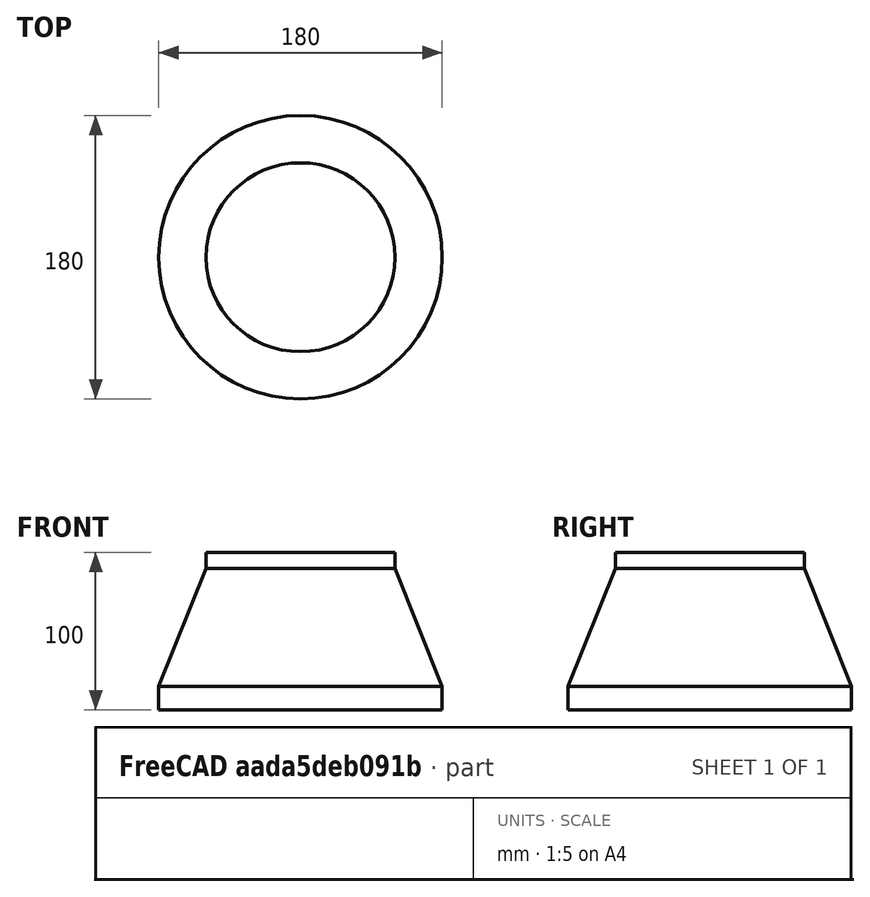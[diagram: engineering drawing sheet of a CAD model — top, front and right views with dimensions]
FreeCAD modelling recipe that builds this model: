
FCSTD DOCUMENT  (FreeCAD 0.19R24366 (Git))
Label: link_0
License: All rights reserved
LicenseURL: http://en.wikipedia.org/wiki/All_rights_reserved
objects: Sketcher::SketchObject×1, PartDesign::Revolution×1, PartDesign::Body×1, Mesh::Feature×1
note: 4 computed .brp shape members not serialized (recipe doc carries the construction recipe); baked Part::Feature solids carry a one-line shape summary decoded from their .brp

FEATURE [Sketcher::SketchObject] Sketch
  FullyConstrained = true
  MapMode = 5
  Placement = pos=(0,0,0) rot=(1,0,0;1.5708rad)
  Support = -> [XZ_Plane]
  sketch-geometry (6):
    g0: LineSegment StartX=1e-16 StartY=50 StartZ=0 EndX=0 EndY=-50 EndZ=0
    g1: LineSegment StartX=1e-16 StartY=50 StartZ=0 EndX=60 EndY=50 EndZ=0
    g2: LineSegment StartX=60 StartY=50 StartZ=0 EndX=60 EndY=40 EndZ=0
    g3: LineSegment StartX=0 StartY=-50 StartZ=0 EndX=90 EndY=-50 EndZ=0
    g4: LineSegment StartX=90 StartY=-50 StartZ=0 EndX=90 EndY=-35 EndZ=0
    g5: LineSegment StartX=90 StartY=-35 StartZ=0 EndX=60 EndY=40 EndZ=0
  constraints (17):
    c: Symmetric(g0,g0,g-1)
    c: PointOnObject(g0,g-2)
    c: DistanceY(g0,g0) = 100
    c: Coincident(g1,g0)
    c: Horizontal(g1)
    c: DistanceX(g1,g1) = 60
    c: Coincident(g2,g1)
    c: Vertical(g2)
    c: Horizontal(g3)
    c: Vertical(g4)
    c: Coincident(g5,g2)
    c: DistanceX(g3,g3) = 90
    c: Coincident(g3,g0)
    c: Coincident(g4,g3)
    c: Coincident(g5,g4)
    c: DistanceY(g2,g2) = 10
    c: DistanceY(g4,g4) = 15
FEATURE [PartDesign::Revolution] Revolution
  AllowMultiFace = false
  Angle = 360
  Axis = (0,-2e-16,1)
  Base = (0,0,0)
  Placement = pos=(0,0,0) rot=(1,0,0;1.5708rad)
  Profile = -> Sketch
  ReferenceAxis = -> Sketch [V_Axis]
  Reversed = true
FEATURE [PartDesign::Body] Body
  Group = -> [Sketch,Revolution]
  Origin = -> Origin
  Placement = pos=(0,0,50) rot=(0,0,1;0rad)
  Tip = -> Revolution
FEATURE [Mesh::Feature] Mesh  label="Body (Meshed)"
